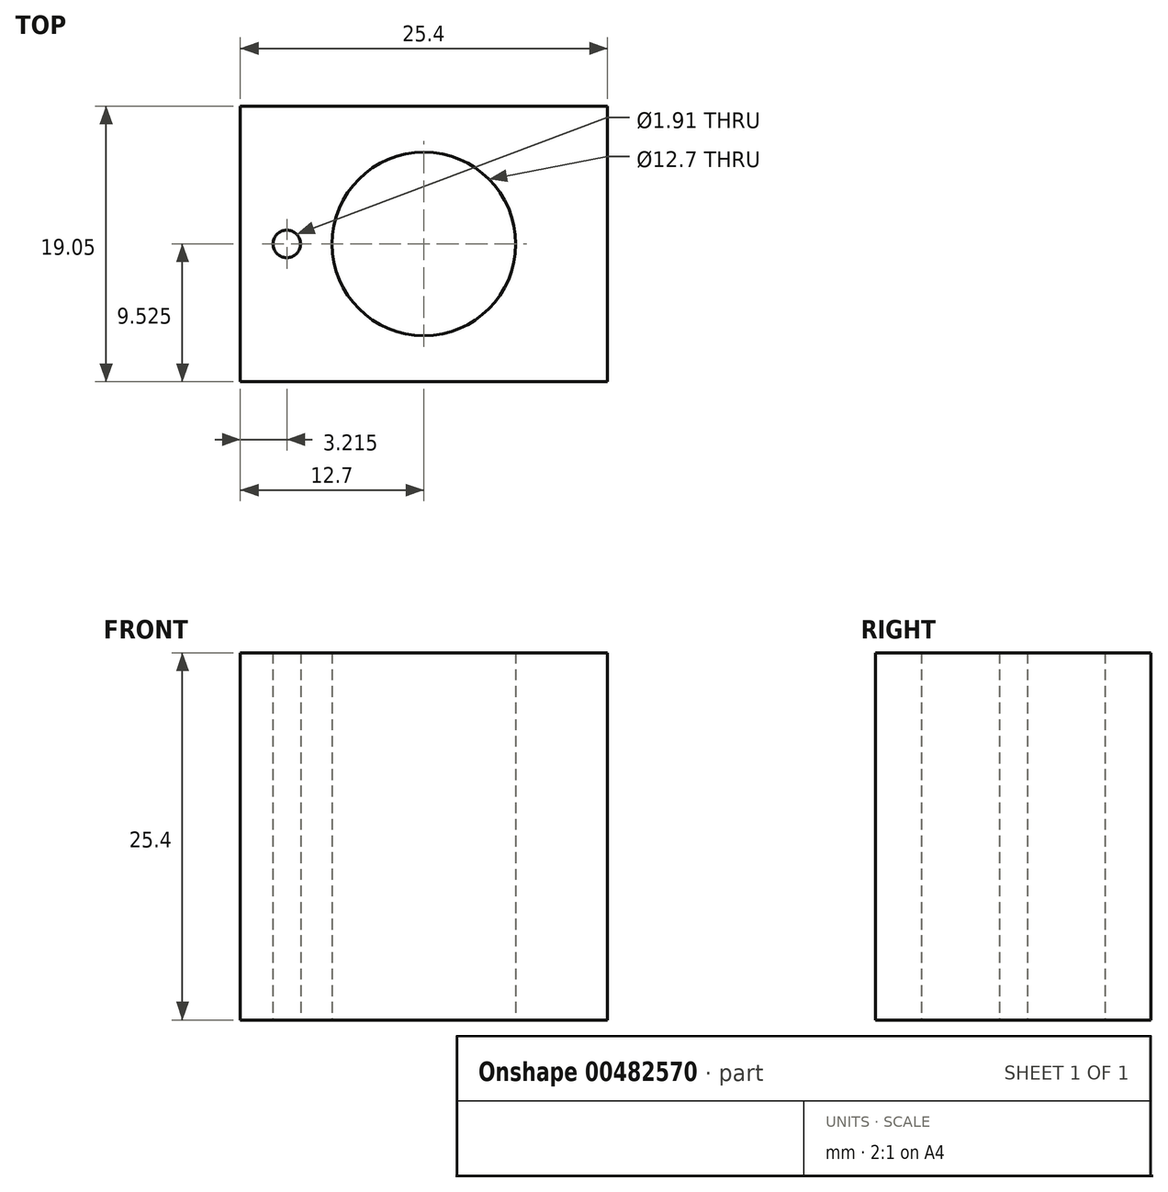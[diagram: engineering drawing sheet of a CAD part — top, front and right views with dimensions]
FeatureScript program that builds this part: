
annotation { "Feature Type Name" : "Feature", "Feature Type Description" : "" }
export const myFeature = defineFeature(function(context is Context, id is Id, definition is map)
    precondition{}
    {
        {
            var Q0;
            Q0=qCreatedBy(makeId("Top.planeOp"),FACE);
            var sketch = newSketch(context, id + "F0", { "sketchPlane" : qUnion([Q0])});
            skLineSegment(sketch, "E0.bottom", {"start": v(0, 0) * mm, "end": v(25.4, 0) * mm});
            skLineSegment(sketch, "E0.top", {"start": v(0, 19.05) * mm, "end": v(25.4, 19.05) * mm});
            skLineSegment(sketch, "E0.left", {"start": v(0, 0) * mm, "end": v(0, 19.05) * mm});
            skLineSegment(sketch, "E0.right", {"start": v(25.4, 0) * mm, "end": v(25.4, 19.05) * mm});
            skCircle(sketch, "E1", {"center": v(12.7, 9.52) * mm, "radius": 6.35 * mm});
            skLineSegment(sketch, "E2", {"start": v(12.7, 9.52) * mm, "end": v(12.7, 19.05) * mm, "construction": true});
            skLineSegment(sketch, "E3", {"start": v(12.7, 9.52) * mm, "end": v(12.7, 0) * mm, "construction": true});
            skLineSegment(sketch, "E4", {"start": v(0, 9.52) * mm, "end": v(12.7, 9.52) * mm, "construction": true});
            skLineSegment(sketch, "E5", {"start": v(25.4, 9.53) * mm, "end": v(12.7, 9.53) * mm, "construction": true});
            skCircle(sketch, "E6", {"center": v(3.22, 9.52) * mm, "radius": 0.95 * mm});
            skLineSegment(sketch, "E7", {"start": v(6.35, 9.52) * mm, "end": v(3.22, 9.52) * mm});
            skSolve(sketch);
        }
        {
            var Q0;
            Q0=makeQuery(id+"F0.imprint","IMPRINT",FACE,{"disambiguationData":[TD([[makeQuery(id+"F0.imprint","IMPRINT",EDGE,{"derivedFrom":sQuery(id+"F0.wireOp",EDGE,"E0.bottom")}),1.0]])]});
            extrude(context, id + "F1", {"entities" : qUnion([Q0]), "depth" : 25.4 * mm});
        }
    });
